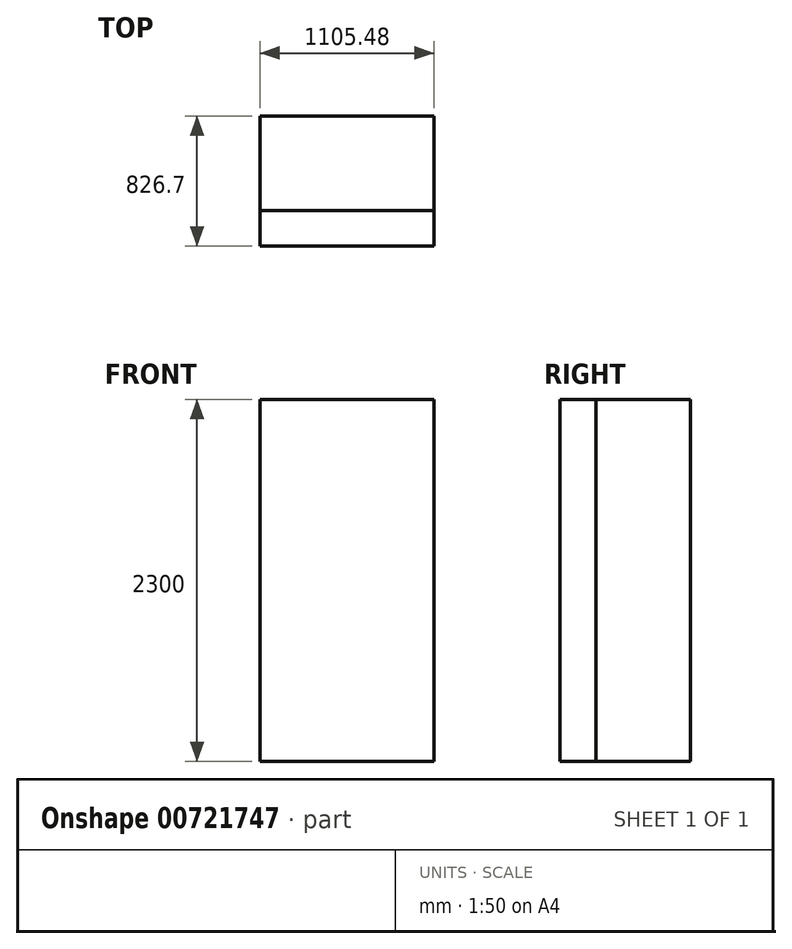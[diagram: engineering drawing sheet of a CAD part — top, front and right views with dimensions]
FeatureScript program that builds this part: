
annotation { "Feature Type Name" : "Feature", "Feature Type Description" : "" }
export const myFeature = defineFeature(function(context is Context, id is Id, definition is map)
    precondition{}
    {
        {
            var Q0;
            Q0=qCreatedBy(makeId("Top.planeOp"),FACE);
            var sketch = newSketch(context, id + "F0", { "sketchPlane" : qUnion([Q0])});
            skLineSegment(sketch, "E0.bottom", {"start": v(127.74, 113.35) * mm, "end": v(-127.74, 113.35) * mm});
            skLineSegment(sketch, "E0.top", {"start": v(127.74, -113.35) * mm, "end": v(-127.74, -113.35) * mm});
            skLineSegment(sketch, "E0.left", {"start": v(127.74, 113.35) * mm, "end": v(127.74, -113.35) * mm});
            skLineSegment(sketch, "E0.right", {"start": v(-127.74, 113.35) * mm, "end": v(-127.74, -113.35) * mm});
            skPoint(sketch, "E0.middle", {"position": v(0, 0) * mm});
            skSolve(sketch);
        }
        {
            var Q0;
            Q0=makeQuery(id+"F0.imprint","IMPRINT",FACE,{"disambiguationData":[TD([[makeQuery(id+"F0.imprint","IMPRINT",EDGE,{"derivedFrom":sQuery(id+"F0.wireOp",EDGE,"E0.bottom")}),1.0]])]});
            extrude(context, id + "F1", {"entities" : qUnion([Q0]), "depth" : 2300 * mm, "offsetDistance" : 25 * mm});
        }
        {
            var Q0;
            Q0=makeQuery(id+"F1.opExtrude","SWEPT_FACE",FACE,{"disambiguationData":[OSD([sQuery(id+"F0.wireOp",EDGE,"E0.left")])]});
            extrude(context, id + "F2", {"entities" : qUnion([Q0]), "operationType" : NewBodyOperationType.ADD, "depth" : 850 * mm, "offsetDistance" : 25 * mm});
        }
        {
            var Q0;
            {var subQ0=sQuery(id+"F0.wireOp",EDGE,"E0.bottom");Q0=makeQuery(id+"F2.boolean.opBoolean","MERGE",FACE,{"derivedFrom":[makeQuery(id+"F1.opExtrude","SWEPT_FACE",FACE,{"disambiguationData":[OSD([subQ0])]}),makeQuery(id+"F2.opExtrude","SWEPT_FACE",FACE,{"disambiguationData":[OSD([subQ0,sQuery(id+"F0.wireOp",EDGE,"E0.left")])]})]});}
            extrude(context, id + "F3", {"entities" : qUnion([Q0]), "depth" : 600 * mm, "offsetDistance" : 25 * mm});
        }
    });
